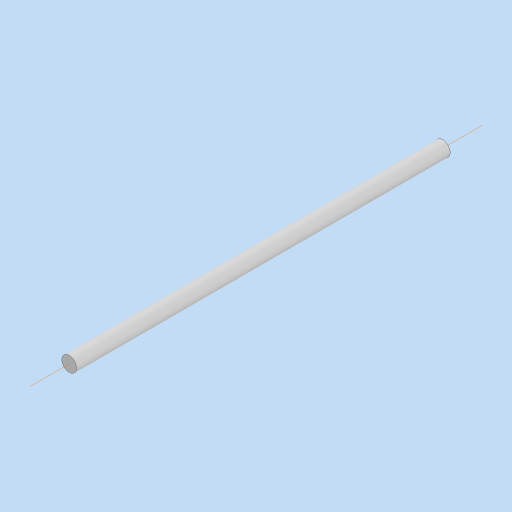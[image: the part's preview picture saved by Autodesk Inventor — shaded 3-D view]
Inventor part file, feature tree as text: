
AUTODESK INVENTOR PART (.ipt)
format: ipt  version: 2024 (Build 280153000, 153)  size: 82,944 bytes
history: native  units: in
note: dims shown in document units (in); Inventor stores cm internally (conversion verified against a paired STEP export)
features: extrude x1, sketch x1
ambient origin geometry x8: Origin, YZ Plane, XZ Plane, XY Plane, X Axis, Y Axis, Z Axis, Center Point
bodies: Solid1 (feature_tree)
feature tree (2):
  extrude  "Extrusion1"  Depth=8.0in TaperAngle=0.0deg
  sketch  "Sketch1"  dims[d0=0.315in d1=8.0in d2=0.0in]
